# Revit family: Sarlam_Lighting_Bollard_light_Chartres_Infini_T2_Diam_420mm_3000_Lm
name_source: partatom
category: Luminaires
units: mm (PartAtom-declared; Revit-internal decimal feet)

## family parameters
Basée sur le plan de construction = Non
Cote de connecteur circulaire = Utiliser le diamètre
Couper avec des vides une fois chargée = Non
Partagée = Non
Point de calcul de pièce = Non
Source d'éclairage = Non
Toujours verticalement = Oui
Type d'élément = Normal

## types (12) — shared parameters
Colour rendering index CRI = 80-89
Colour temperature K MAX = 4000
Colour temperature K MIN = 4000
Degree of protection (IP) = IP55
Effective luminous flux lm = 3000
Fabricant = LEGRAND
General Conditions of Use = https://export.legrand.com
Height/depth = 90 mm  [stored 0.295276 ft]
Impact strength (IK) = IK10
Lamp holder = None
Lamp power at multiwatt = 21/39W
Lamp type = LED not exchangeable
Length = 420 mm  [stored 1.37795 ft]
Light sharing = Symmetric
Material housing = Plastique
Nominal voltage (Un) V MAX = 253
Nominal voltage (Un) V MIN = 207
Outer diameter = 420 mm  [stored 1.37795 ft]
Protection Class = II
Radiation angle = Open beam
Type of control gear = LED operating device current-controlled
URL = http://www.legrandoc.com
URL Bulkhead = http://www.legrandoc.com
Voltage type = AC
Width = 420 mm  [stored 1.37795 ft]
zero-valued in all types: Elévation par défaut, Nominal current mA MAX, Nominal current mA MIN, System power W

## per-type parameters (varying)
| type | Bollard light Height | Bulkhead | Colour housing | Description | Leg Height | Modèle | Type of dimming | With light sensor | With movement sensor |
| Bollard light 600 + ON/OFF WHITE | 600 mm | Legrand-Lighting-Bulkhead-Chartres Infini-T2 Diam 420mm-3000Lm : ON/OFF WHITE | LEGRAND - White | BOLLARD LIGHT CHARTRES INFINI HEIGHT 600 + CHARTRES INFINI 3000LM 4000K STANDARD ON/OFF WHITE | 524 mm | SL-532030 + SL-532009 | Not dimmable | Non | Non |
| Bollard light 1200 + ON/OFF WHITE | 1200 mm | Legrand-Lighting-Bulkhead-Chartres Infini-T2 Diam 420mm-3000Lm : ON/OFF WHITE | LEGRAND - White | BOLLARD LIGHT CHARTRES INFINI HEIGHT 1200 + CHARTRES INFINI 3000LM 4000K STANDARD ON/OFF WHITE | 1124 mm  [stored 3.68766 ft] | SL-532033 + SL-532009 | Not dimmable | Non | Non |
| Bollard light 600 + ON/OFF ANTHRACITE | 600 mm | Legrand-Lighting-Bulkhead-Chartres Infini-T2 Diam 420mm-3000Lm : ON/OFF ANTHRACITE | LEGRAND - Anthracite | BOLLARD LIGHT CHARTRES INFINI HEIGHT 600 + CHARTRES INFINI 3000LM 4000K STANDARD ON/OFF BLACK | 524 mm | SL-532031 + SL-532010 | Not dimmable | Non | Non |
| Bollard light 1200 + ON/OFF ANTHRACITE | 1200 mm | Legrand-Lighting-Bulkhead-Chartres Infini-T2 Diam 420mm-3000Lm : ON/OFF ANTHRACITE | LEGRAND - Anthracite | BOLLARD LIGHT CHARTRES INFINI HEIGHT 1200 + CHARTRES INFINI 3000LM 4000K STANDARD ON/OFF BLACK | 1124 mm  [stored 3.68766 ft] | SL-532034 + SL-532010 | Not dimmable | Non | Non |
| Bollard light 600 + ON/OFF GREY METAL | 600 mm | Legrand-Lighting-Bulkhead-Chartres Infini-T2 Diam 420mm-3000Lm : ON/OFF GREY METAL | LEGRAND - Grey | BOLLARD LIGHT CHARTRES INFINI HEIGHT 600 + CHARTRES INFINI 3000LM 4000K STANDARD ON/OFF SILVER | 524 mm | SL-532032 + SL-532011 | Not dimmable | Non | Non |
| Bollard light 1200 + ON/OFF GREY METAL | 1200 mm | Legrand-Lighting-Bulkhead-Chartres Infini-T2 Diam 420mm-3000Lm : ON/OFF GREY METAL | LEGRAND - Grey | BOLLARD LIGHT CHARTRES INFINI HEIGHT 1200 + CHARTRES INFINI 3000LM 4000K STANDARD ON/OFF SILVER | 1124 mm  [stored 3.68766 ft] | SL-532035 + SL-532011 | Not dimmable | Non | Non |
| Bollard light 600 + With microwave sensor WHITE | 600 mm | Legrand-Lighting-Bulkhead-Chartres Infini-T2 Diam 420mm-3000Lm : With microwave sensor WHITE | LEGRAND - White | BOLLARD LIGHT CHARTRES INFINI HEIGHT 600 + CHARTRES INFINI 3000LM 4000K  STANDARD HF DETECTION WHITE | 524 mm | SL-532030 + SL-532049 | Other | Oui | Oui |
| Bollard light 1200 + With microwave sensor WHITE | 1200 mm | Legrand-Lighting-Bulkhead-Chartres Infini-T2 Diam 420mm-3000Lm : With microwave sensor WHITE | LEGRAND - White | BOLLARD LIGHT CHARTRES INFINI HEIGHT 1200 + CHARTRES INFINI 3000LM 4000K  STANDARD HF DETECTION WHITE | 1124 mm  [stored 3.68766 ft] | SL-532033 + SL-532049 | Other | Oui | Oui |
| Bollard light 600 + With microwave sensor ANTHRACITE | 600 mm | Legrand-Lighting-Bulkhead-Chartres Infini-T2 Diam 420mm-3000Lm : With microwave sensor ANTHRACITE | LEGRAND - Anthracite | BOLLARD LIGHT CHARTRES INFINI HEIGHT 600 + CHARTRES INFINI 3000LM 4000K  STANDARD HF DETECTION BLACK | 524 mm | SL-532031 + SL-532050 | Other | Oui | Oui |
| Bollard light 1200 + With microwave sensor ANTHRACITE | 1200 mm | Legrand-Lighting-Bulkhead-Chartres Infini-T2 Diam 420mm-3000Lm : With microwave sensor ANTHRACITE | LEGRAND - Anthracite | BOLLARD LIGHT CHARTRES INFINI HEIGHT 1200 + CHARTRES INFINI 3000LM 4000K  STANDARD HF DETECTION BLACK | 1124 mm  [stored 3.68766 ft] | SL-532034 + SL-532050 | Other | Oui | Oui |
| Bollard light 600 + With microwave sensor GREY METAL | 600 mm | Legrand-Lighting-Bulkhead-Chartres Infini-T2 Diam 420mm-3000Lm : With microwave sensor GREY METAL | LEGRAND - Grey | BOLLARD LIGHT CHARTRES INFINI HEIGHT 600 + CHARTRES INFINI 3000LM 4000K  STANDARD HF DETECTION SILVER | 524 mm | SL-532032 + SL-532051 | Other | Oui | Oui |
| Bollard light 1200 + With microwave sensor GREY METAL | 1200 mm | Legrand-Lighting-Bulkhead-Chartres Infini-T2 Diam 420mm-3000Lm : With microwave sensor GREY METAL | LEGRAND - Grey | BOLLARD LIGHT CHARTRES INFINI HEIGHT 1200 + CHARTRES INFINI 3000LM 4000K  STANDARD HF DETECTION SILVER | 1124 mm  [stored 3.68766 ft] | SL-532035 + SL-532051 | Other | Oui | Oui |

note: [stored X ft] marks values corroborated as IEEE doubles in the binary element streams (Revit-internal decimal feet)

## geometry (parser evidence)
native form markers: Blend x14
no freeform markers — native parametric forms only
